FCSTD DOCUMENT  (FreeCAD 0.17R13541 (Git))
Label: simple_wire
License: All rights reserved
LicenseURL: http://en.wikipedia.org/wiki/All_rights_reserved
objects: Sketcher::SketchObject×3, Spreadsheet::Sheet×1
note: 3 computed .brp shape members not serialized (recipe doc carries the construction recipe); baked Part::Feature solids carry a one-line shape summary decoded from their .brp

FEATURE [Spreadsheet::Sheet] modelParams
  cells = A1=paramName; B1=paramValue; A2=d_junction; B2(d_junction)=0.10000000000000001; A3=d_spacing; B3(d_spacing)=0.050000000000000003; A4=d_linewidth; B4(d_linewidth)=0.14999999999999999
FEATURE [Sketcher::SketchObject] Sketch003  label="sim_domain"
  sketch-geometry (4):
    g0: LineSegment StartX=-1 StartY=-0.5 StartZ=0 EndX=1 EndY=-0.5 EndZ=0
    g1: LineSegment StartX=1 StartY=-0.5 StartZ=0 EndX=1 EndY=0.5 EndZ=0
    g2: LineSegment StartX=1 StartY=0.5 StartZ=0 EndX=-1 EndY=0.5 EndZ=0
    g3: LineSegment StartX=-1 StartY=0.5 StartZ=0 EndX=-1 EndY=-0.5 EndZ=0
  constraints (12):
    c: Coincident(g0,g1)
    c: Coincident(g1,g2)
    c: Coincident(g2,g3)
    c: Coincident(g3,g0)
    c: Horizontal(g0)
    c: Horizontal(g2)
    c: Vertical(g1)
    c: Vertical(g3)
    c: DistanceX(g2,g-1) = 1
    c: DistanceX(g-1,g1) = 1
    c: DistanceY(g0,g-1) = 0.5
    c: DistanceY(g-1,g2) = 0.5
FEATURE [Sketcher::SketchObject] Sketch002  label="wire"
  ExternalGeometry = -> [Sketch003]
  sketch-geometry (4):
    g0: LineSegment StartX=-0.5 StartY=0.05 StartZ=0 EndX=0.5 EndY=0.05 EndZ=0
    g1: LineSegment StartX=0.5 StartY=0.05 StartZ=0 EndX=0.5 EndY=-0.05 EndZ=0
    g2: LineSegment StartX=0.5 StartY=-0.05 StartZ=0 EndX=-0.5 EndY=-0.05 EndZ=0
    g3: LineSegment StartX=-0.5 StartY=-0.05 StartZ=0 EndX=-0.5 EndY=0.05 EndZ=0
  constraints (12):
    c: Coincident(g0,g1)
    c: Coincident(g1,g2)
    c: Coincident(g2,g3)
    c: Coincident(g3,g0)
    c: Horizontal(g0)
    c: Horizontal(g2)
    c: Vertical(g1)
    c: Vertical(g3)
    c: DistanceX(g-3,g0) = 0.5
    c: DistanceX(g0,g-4) = 0.5
    c: DistanceY(g-1,g0) = 0.05
    c: DistanceY(g2,g-1) = 0.05
FEATURE [Sketcher::SketchObject] Sketch
  ExternalGeometry = -> [Sketch003]
  sketch-geometry (4):
    g0: LineSegment StartX=-0.75 StartY=0.25 StartZ=0 EndX=0.75 EndY=0.25 EndZ=0
    g1: LineSegment StartX=0.75 StartY=0.25 StartZ=0 EndX=0.75 EndY=-0.25 EndZ=0
    g2: LineSegment StartX=0.75 StartY=-0.25 StartZ=0 EndX=-0.75 EndY=-0.25 EndZ=0
    g3: LineSegment StartX=-0.75 StartY=-0.25 StartZ=0 EndX=-0.75 EndY=0.25 EndZ=0
  constraints (12):
    c: Coincident(g0,g1)
    c: Coincident(g1,g2)
    c: Coincident(g2,g3)
    c: Coincident(g3,g0)
    c: Horizontal(g0)
    c: Horizontal(g2)
    c: Vertical(g1)
    c: Vertical(g3)
    c: DistanceX(g-3,g0) = 0.25
    c: DistanceY(g-3,g2) = 0.25
    c: DistanceY(g0,g-3) = 0.25
    c: DistanceX(g1,g-4) = 0.25
